annotation { "Feature Type Name" : "Feature", "Feature Type Description" : "" }
export const myFeature = defineFeature(function(context is Context, id is Id, definition is map)
    precondition{}
    {
        {
            var Q0;
            Q0=qCreatedBy(makeId("Front.planeOp"),FACE);
            var sketch = newSketch(context, id + "F0", { "sketchPlane" : qUnion([Q0])});
            skLineSegment(sketch, "E0.bottom", {"start": v(-71.35, 39.82) * mm, "end": v(-29.31, 39.82) * mm});
            skLineSegment(sketch, "E0.top", {"start": v(-71.35, -28.02) * mm, "end": v(-29.31, -28.02) * mm});
            skLineSegment(sketch, "E0.left", {"start": v(-71.35, 39.82) * mm, "end": v(-71.35, -28.02) * mm});
            skLineSegment(sketch, "E0.right", {"start": v(-29.31, 39.82) * mm, "end": v(-29.31, -28.02) * mm});
            skLineSegment(sketch, "E1", {"start": v(-61.02, -28.02) * mm, "end": v(-56.24, -51.07) * mm});
            skLineSegment(sketch, "E2", {"start": v(-48.3, -28.02) * mm, "end": v(-56.24, -51.07) * mm});
            skLineSegment(sketch, "E3", {"start": v(-56.24, -51.07) * mm, "end": v(-26.36, -51.07) * mm});
            skText(sketch, "E4", { "text": "Solar Panel\n", "fontName": "OpenSans-Regular.ttf"});
            skText(sketch, "E5", { "text": "Wires\n", "fontName": "OpenSans-Regular.ttf"});
            skLineSegment(sketch, "E6.bottom", {"start": v(42.7, -5.02) * mm, "end": v(97.95, -5.02) * mm});
            skLineSegment(sketch, "E6.top", {"start": v(42.7, -52.15) * mm, "end": v(97.95, -52.15) * mm});
            skLineSegment(sketch, "E6.left", {"start": v(42.7, -5.02) * mm, "end": v(42.7, -52.15) * mm});
            skLineSegment(sketch, "E6.right", {"start": v(97.95, -5.02) * mm, "end": v(97.95, -52.15) * mm});
            skText(sketch, "E7", { "text": "Hot Plate/ Oven/ Stove", "fontName": "OpenSans-Regular.ttf"});
            skText(sketch, "E8", { "text": "8 in", "fontName": "OpenSans-Regular.ttf"});
            skText(sketch, "E9", { "text": "10 in", "fontName": "OpenSans-Regular.ttf"});
            skText(sketch, "E10", { "text": "8 in", "fontName": "OpenSans-Regular.ttf"});
            skText(sketch, "E11", { "text": "8 in", "fontName": "OpenSans-Regular.ttf"});
            skText(sketch, "E12", { "text": "10in", "fontName": "OpenSans-Regular.ttf"});
            skText(sketch, "E13", { "text": "5 in\n", "fontName": "OpenSans-Regular.ttf"});
            skLineSegment(sketch, "E14.bottom", {"start": v(-4.8, -40.37) * mm, "end": v(5.91, -40.37) * mm});
            skLineSegment(sketch, "E14.top", {"start": v(-4.8, -46) * mm, "end": v(5.91, -46) * mm});
            skLineSegment(sketch, "E14.left", {"start": v(-4.8, -40.37) * mm, "end": v(-4.8, -46) * mm});
            skLineSegment(sketch, "E14.right", {"start": v(5.91, -40.37) * mm, "end": v(5.91, -46) * mm});
            skLineSegment(sketch, "E15", {"start": v(-26.36, -51.07) * mm, "end": v(-4.8, -43.19) * mm});
            skLineSegment(sketch, "E16", {"start": v(6.27, -43.5) * mm, "end": v(42.7, -25.26) * mm});
            skText(sketch, "E17", { "text": "Resistors\n", "fontName": "OpenSans-Regular.ttf"});
            const initialGuessF0  = {"E4": [-0.06397, 0.04277, 1, 0, 0.00295], "E5": [-0.0399, -0.03927, 1, 0, 0.00369], "E7": [0.05249, 0.0052, 1, 0, 0.0022], "E8": [0.0583, -0.06148, 1, 0, 0.00667], "E9": [-0.01563, -0.05932, 1, 0, 0.00608], "E10": [0.10252, -0.033, 1, 0, 0.00534], "E11": [0.062, -0.0035, 1, 0, 0.00534], "E12": [-0.02526, 0.01143, 1, 0, 0.0059], "E13": [-0.05955, 0.04775, 1, 0, 0.00442], "E17": [-0.0072, -0.03392, 1, 0, 0.00277]};
            skSetInitialGuess(sketch, initialGuessF0);
            skSolve(sketch);
        }
        {
            var Q0;
            Q0=makeQuery(id+"F0.imprint","IMPRINT",FACE,{"disambiguationData":[TD([[makeQuery(id+"F0.imprint","IMPRINT",EDGE,{"derivedFrom":sQuery(id+"F0.wireOp",EDGE,"E0.bottom")}),-1.0]])]});
            extrude(context, id + "F1", {"entities" : qUnion([Q0]), "depth" : 0.64 * mm, "offsetDistance" : 25.4 * mm});
        }
        {
            var Q0;
            {var subQ3=sQuery(id+"F0.wireOp",EDGE,"E14.bottom");Q0=makeQuery(id+"F0.imprint","IMPRINT",FACE,{"disambiguationData":[TD([[makeQuery(id+"F0.imprint","IMPRINT",EDGE,{"derivedFrom":subQ3}),-1.0]])]});}
            extrude(context, id + "F2", {"entities" : qUnion([Q0]), "depth" : 3.56 * mm, "offsetDistance" : 25.4 * mm});
        }
        {
            var Q0;
            {var subQ3=sQuery(id+"F0.wireOp",EDGE,"E6.bottom");Q0=makeQuery(id+"F0.imprint","IMPRINT",FACE,{"disambiguationData":[TD([[makeQuery(id+"F0.imprint","IMPRINT",EDGE,{"derivedFrom":subQ3}),-1.0]])]});}
            extrude(context, id + "F3", {"entities" : qUnion([Q0]), "depth" : 2.3 * mm, "offsetDistance" : 25.4 * mm});
        }
    });